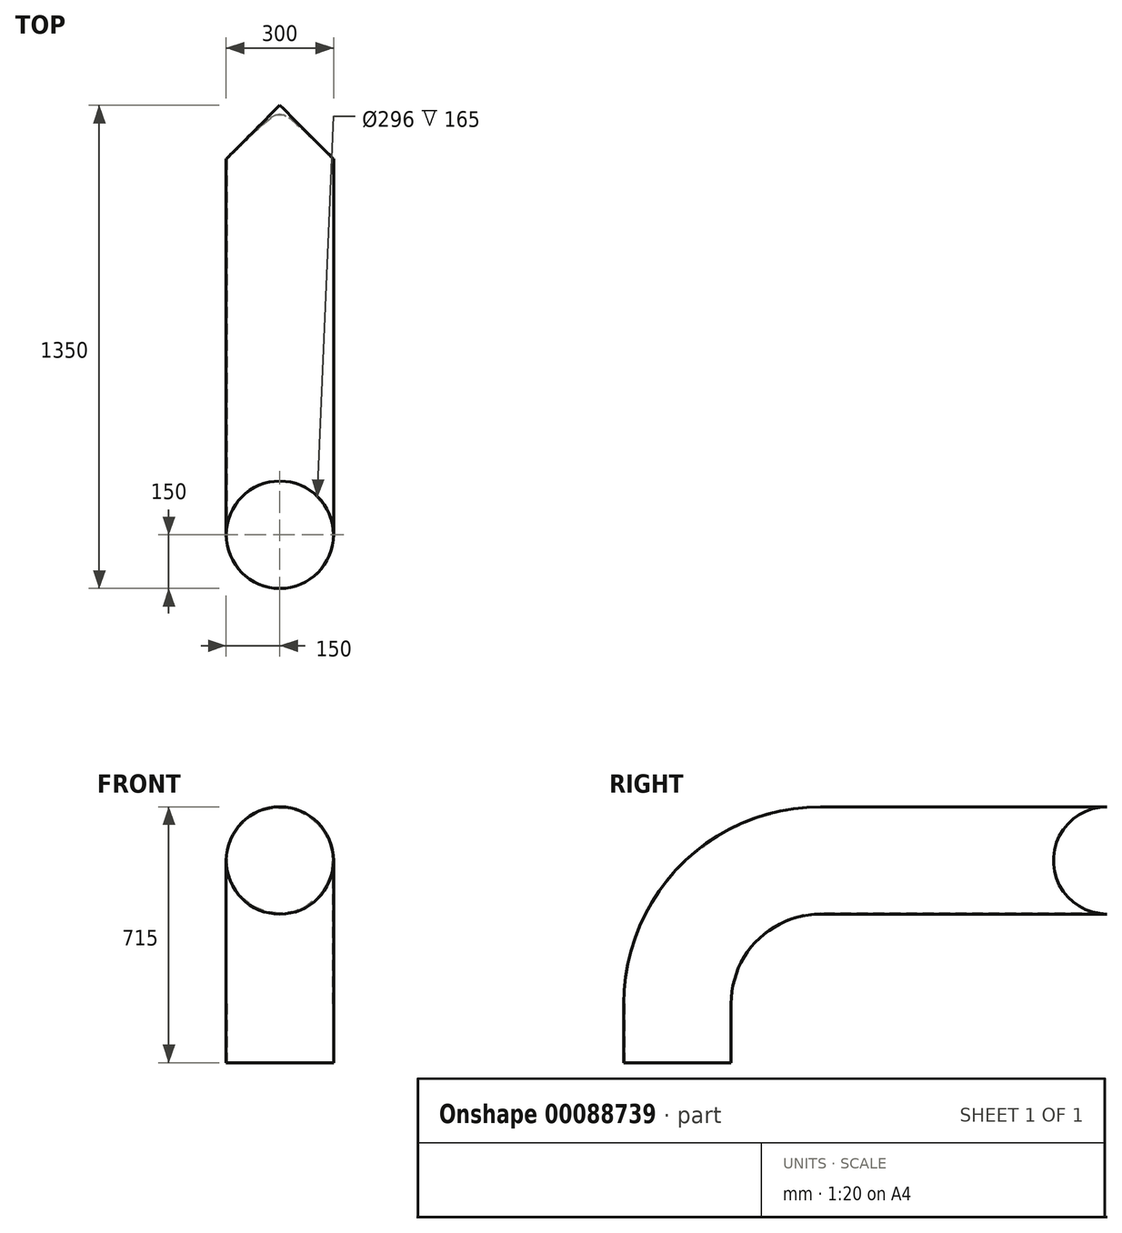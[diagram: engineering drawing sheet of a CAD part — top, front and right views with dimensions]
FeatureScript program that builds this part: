
annotation { "Feature Type Name" : "Feature", "Feature Type Description" : "" }
export const myFeature = defineFeature(function(context is Context, id is Id, definition is map)
    precondition{}
    {
        {
            var Q0;
            Q0=qCreatedBy(makeId("Front.planeOp"),FACE);
            var sketch = newSketch(context, id + "F0", { "sketchPlane" : qUnion([Q0])});
            skCircle(sketch, "E0", {"center": v(0, 0) * mm, "radius": 150 * mm});
            skCircle(sketch, "E1", {"center": v(0, 0) * mm, "radius": 148 * mm});
            skSolve(sketch);
        }
        {
            var Q0;
            Q0=qCreatedBy(makeId("Right.planeOp"),FACE);
            var sketch = newSketch(context, id + "F1", { "sketchPlane" : qUnion([Q0])});
            skLineSegment(sketch, "E2", {"start": v(0, 0) * mm, "end": v(-800, 0) * mm});
            skLineSegment(sketch, "E3", {"start": v(-1200, -400) * mm, "end": v(-1200, -565) * mm});
            skPoint(sketch, "E4.visualSharp", {"position": v(-1200, 0) * mm});
            skArc(sketch, "E4.filletArc", {"start": v(-800, 0) * mm, "mid": v(-1082.84, -117.16) * mm, "end": v(-1200, -400) * mm});
            skPoint(sketch, "E5", {"position": v(0, 0) * mm});
            skCircle(sketch, "E6", {"center": v(0, 0) * mm, "radius": 150 * mm});
            skSolve(sketch);
        }
        {
            var Q0;
            Q0=makeQuery(id+"F0.imprint","IMPRINT",FACE,{"disambiguationData":[TD([[makeQuery(id+"F0.imprint","IMPRINT",EDGE,{"derivedFrom":sQuery(id+"F0.wireOp",EDGE,"E0")}),1.0]])]});
            var Q1;
            Q1=sQuery(id+"F1.wireOp",EDGE,"E2");
            var Q2;
            Q2=sQuery(id+"F1.wireOp",EDGE,"E4.filletArc");
            var Q3;
            Q3=sQuery(id+"F1.wireOp",EDGE,"E3");
            sweep(context, id + "F2", {"profiles" : qUnion([Q0]), "path" : qUnion([Q1, Q2, Q3])});
        }
        {
            var Q0;
            Q0=makeQuery(id+"F1.imprint","IMPRINT",FACE,{"disambiguationData":[TD([[makeQuery(id+"F1.imprint","IMPRINT",EDGE,{"derivedFrom":sQuery(id+"F1.wireOp",EDGE,"E6")}),1.0]])]});
            extrude(context, id + "F3", {"entities" : qUnion([Q0]), "operationType" : NewBodyOperationType.REMOVE, "depth" : 300 * mm, "symmetric" : true});
        }
        {
            var Q0;
            Q0=qCreatedBy(makeId("Front.planeOp"),FACE);
            var sketch = newSketch(context, id + "F4", { "sketchPlane" : qUnion([Q0])});
            skCircle(sketch, "E7", {"center": v(0, -7129.13) * mm, "radius": 200 * mm});
            skSolve(sketch);
        }
        {
            var Q0;
            Q0=makeQuery(id+"F4.imprint","IMPRINT",FACE,{"disambiguationData":[TD([[makeQuery(id+"F4.imprint","IMPRINT",EDGE,{"derivedFrom":sQuery(id+"F4.wireOp",EDGE,"E7")}),1.0]])]});
            extrude(context, id + "F5", {"entities" : qUnion([Q0]), "operationType" : NewBodyOperationType.REMOVE, "endBound" : BoundingType.THROUGH_ALL, "depth" : 25 * mm});
        }
    });
